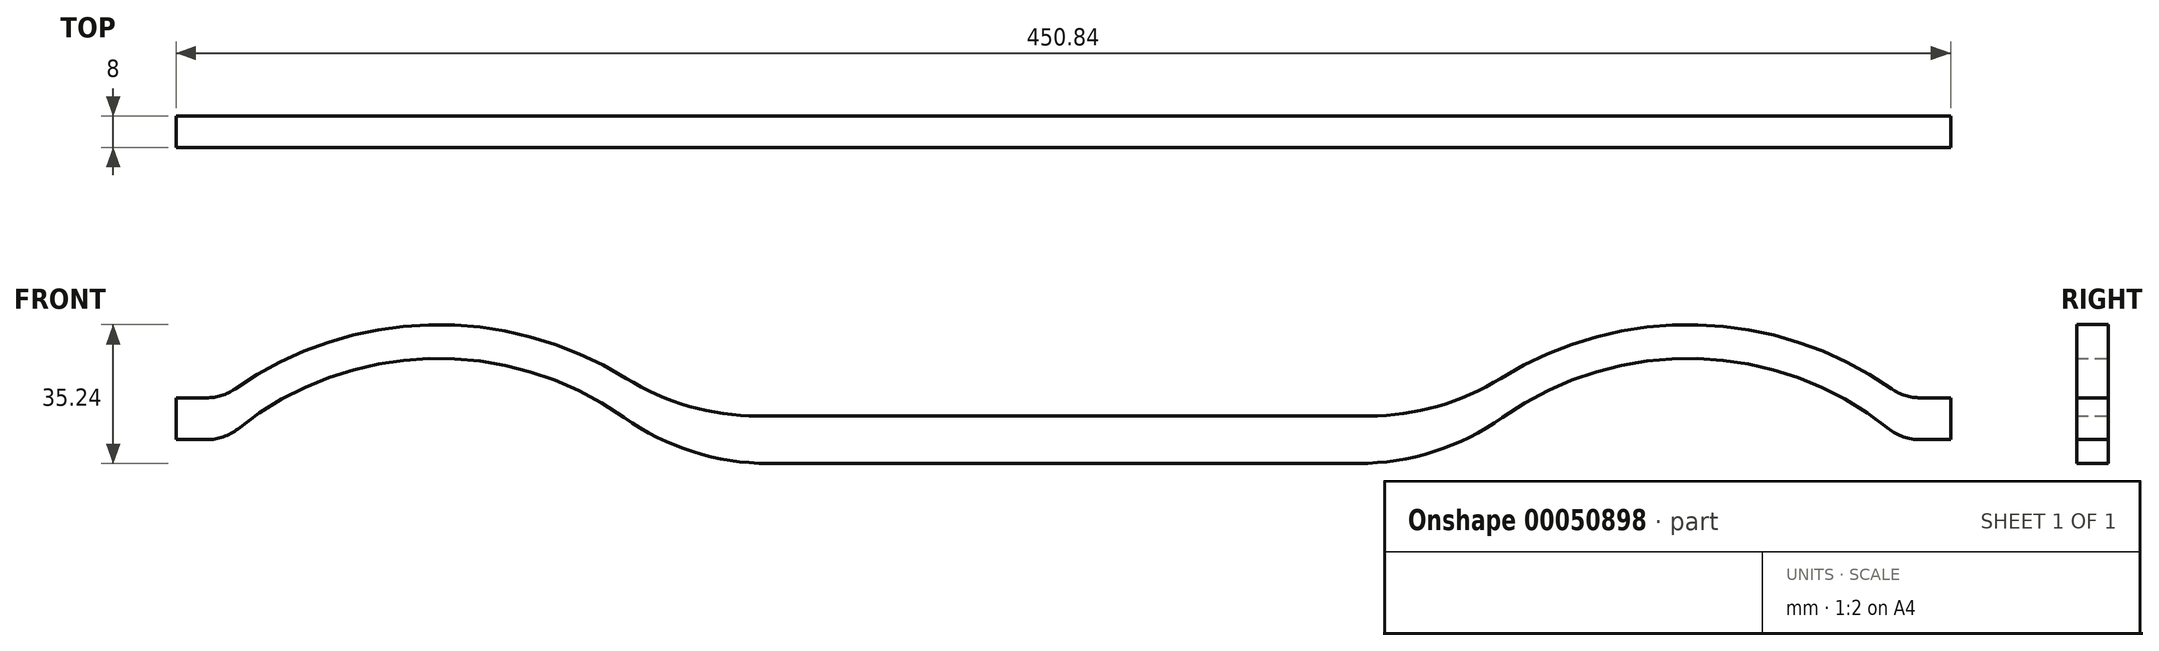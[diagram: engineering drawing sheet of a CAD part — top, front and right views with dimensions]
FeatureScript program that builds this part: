
annotation { "Feature Type Name" : "Feature", "Feature Type Description" : "" }
export const myFeature = defineFeature(function(context is Context, id is Id, definition is map)
    precondition{}
    {
        {
            var Q0;
            Q0=qCreatedBy(makeId("Front.planeOp"),FACE);
            var sketch = newSketch(context, id + "F0", { "sketchPlane" : qUnion([Q0])});
            skLineSegment(sketch, "E0.rect.bottom", {"start": v(77.6, 6.03) * mm, "end": v(-77.6, 6.03) * mm});
            skLineSegment(sketch, "E0.rect.top", {"start": v(74.9, -6.03) * mm, "end": v(-74.9, -6.03) * mm});
            skPoint(sketch, "E0.rect.middle", {"position": v(0, 0) * mm});
            skArc(sketch, "E1", {"start": v(210.45, 12.92) * mm, "mid": v(161.2, 29.18) * mm, "end": v(111.13, 15.6) * mm});
            skPoint(sketch, "E1.second.point", {"position": v(122.72, -143.62) * mm});
            skPoint(sketch, "E1.third.point", {"position": v(233.72, -10.86) * mm});
            skArc(sketch, "E2.MirrorC", {"start": v(-210.45, 12.92) * mm, "mid": v(-161.2, 29.18) * mm, "end": v(-111.13, 15.6) * mm});
            skArc(sketch, "E3", {"start": v(209.7, 2.78) * mm, "mid": v(161.13, 20.61) * mm, "end": v(111.6, 5.64) * mm});
            skArc(sketch, "E4", {"start": v(-111.6, 5.64) * mm, "mid": v(-161.13, 20.61) * mm, "end": v(-209.7, 2.78) * mm});
            skLineSegment(sketch, "E5", {"start": v(-225.2, 0) * mm, "end": v(-225.43, 0) * mm});
            skLineSegment(sketch, "E6", {"start": v(-225.43, 0) * mm, "end": v(-225.43, 10.62) * mm});
            skLineSegment(sketch, "E7", {"start": v(-225.43, 10.62) * mm, "end": v(-217.73, 10.62) * mm});
            skLineSegment(sketch, "E8.MirrorCS", {"start": v(225.43, 0) * mm, "end": v(225.43, 10.62) * mm});
            skLineSegment(sketch, "E9.MirrorCS", {"start": v(225.43, 10.62) * mm, "end": v(217.73, 10.62) * mm});
            skLineSegment(sketch, "E10.MirrorCS", {"start": v(225.2, 0) * mm, "end": v(225.43, 0) * mm});
            skLineSegment(sketch, "E11", {"start": v(-225.2, 0) * mm, "end": v(-217.64, 0) * mm});
            skLineSegment(sketch, "E12", {"start": v(225.2, 0) * mm, "end": v(217.64, 0) * mm});
            skPoint(sketch, "E13.visualSharp", {"position": v(98.4, 6.03) * mm});
            skArc(sketch, "E13.filletArc", {"start": v(77.6, 6.03) * mm, "mid": v(95.03, 8.47) * mm, "end": v(111.13, 15.6) * mm});
            skPoint(sketch, "E14.visualSharp", {"position": v(-98.4, 6.03) * mm});
            skArc(sketch, "E14.filletArc", {"start": v(-111.13, 15.6) * mm, "mid": v(-95.03, 8.47) * mm, "end": v(-77.6, 6.03) * mm});
            skPoint(sketch, "E15.visualSharp", {"position": v(-98.4, -6.03) * mm});
            skArc(sketch, "E15.filletArc", {"start": v(-111.6, 5.64) * mm, "mid": v(-94.15, -3.04) * mm, "end": v(-74.9, -6.03) * mm});
            skPoint(sketch, "E16.visualSharp", {"position": v(98.4, -6.03) * mm});
            skArc(sketch, "E16.filletArc", {"start": v(74.9, -6.03) * mm, "mid": v(94.15, -3.04) * mm, "end": v(111.6, 5.64) * mm});
            skPoint(sketch, "E17.visualSharp", {"position": v(213, 0) * mm});
            skArc(sketch, "E17.filletArc", {"start": v(209.7, 2.78) * mm, "mid": v(213.44, 0.72) * mm, "end": v(217.64, 0) * mm});
            skPoint(sketch, "E18.visualSharp", {"position": v(-213, 0) * mm});
            skArc(sketch, "E18.filletArc", {"start": v(-217.64, 0) * mm, "mid": v(-213.44, 0.72) * mm, "end": v(-209.7, 2.78) * mm});
            skPoint(sketch, "E19.visualSharp", {"position": v(-213.58, 10.62) * mm});
            skArc(sketch, "E19.filletArc", {"start": v(-217.73, 10.62) * mm, "mid": v(-213.91, 11.2) * mm, "end": v(-210.45, 12.92) * mm});
            skPoint(sketch, "E20.visualSharp", {"position": v(213.58, 10.62) * mm});
            skArc(sketch, "E20.filletArc", {"start": v(210.45, 12.92) * mm, "mid": v(213.91, 11.2) * mm, "end": v(217.73, 10.62) * mm});
            skSolve(sketch);
        }
        {
            var Q0;
            Q0 = qSketchRegion(id + "F0", true);
            extrude(context, id + "F1", {"entities" : qUnion([Q0]), "endBound" : BoundingType.SYMMETRIC, "depth" : 8 * mm});
        }
    });
